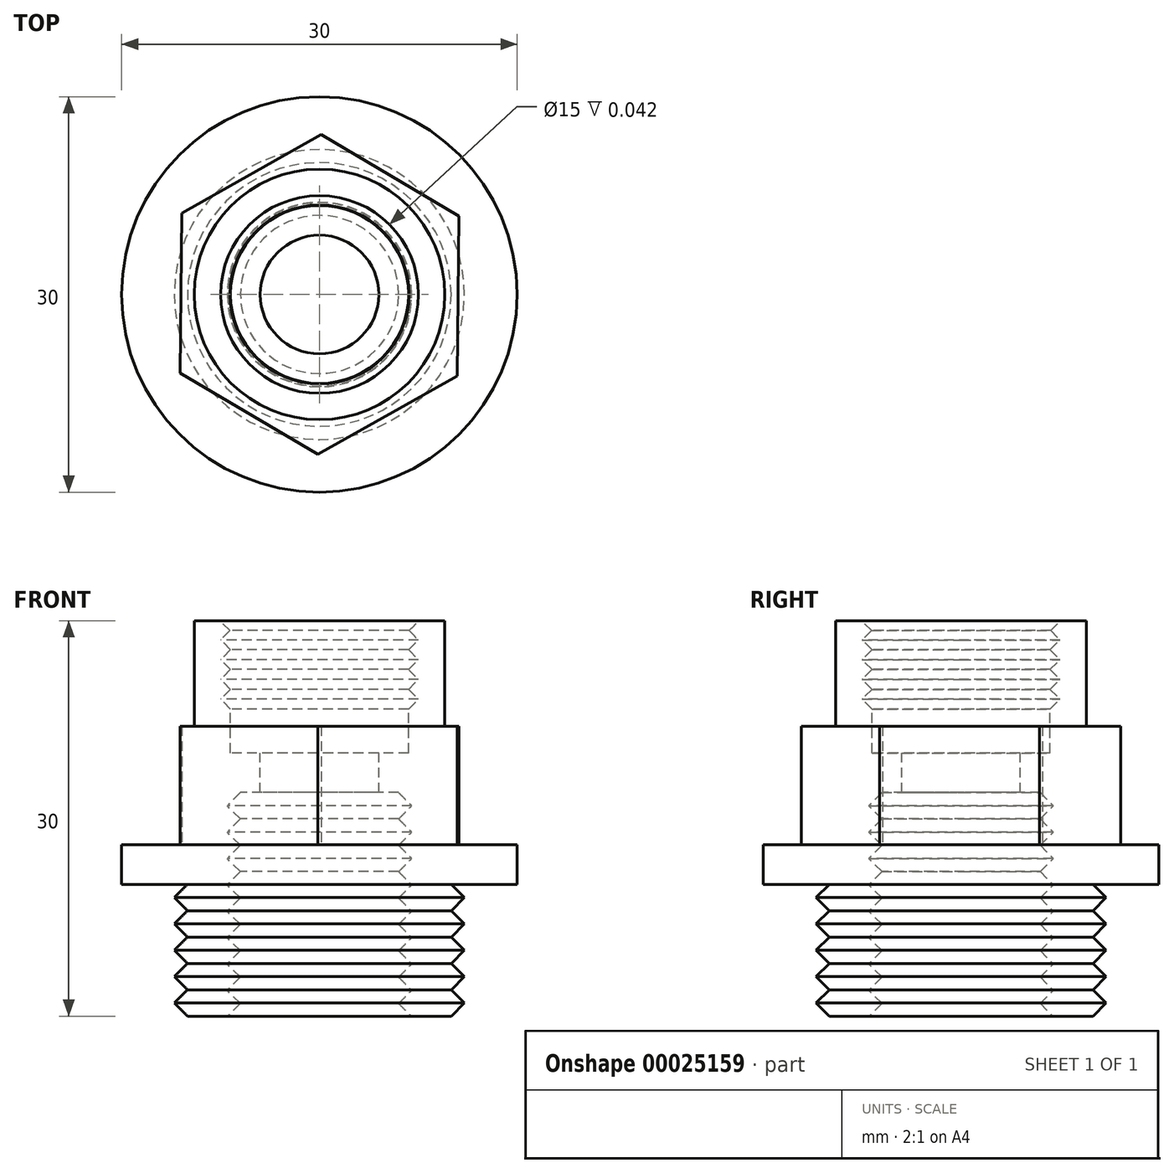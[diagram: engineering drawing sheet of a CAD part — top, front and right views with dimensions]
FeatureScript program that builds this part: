
annotation { "Feature Type Name" : "Feature", "Feature Type Description" : "" }
export const myFeature = defineFeature(function(context is Context, id is Id, definition is map)
    precondition{}
    {
        {
            var Q0;
            Q0=qCreatedBy(makeId("Front.planeOp"),FACE);
            var sketch = newSketch(context, id + "F0", { "sketchPlane" : qUnion([Q0])});
            skLineSegment(sketch, "E0", {"start": v(-0.01, -0.04) * mm, "end": v(-0.01, 28.34) * mm});
            skLineSegment(sketch, "E1", {"start": v(-0.01, -0.04) * mm, "end": v(-6.01, -0.04) * mm});
            skLineSegment(sketch, "E2", {"start": v(-10.01, 28.34) * mm, "end": v(-11.01, 27.34) * mm});
            skLineSegment(sketch, "E3.0.1.0", {"start": v(-11.01, 27.34) * mm, "end": v(-10.01, 26.34) * mm});
            skLineSegment(sketch, "E3.0.2.0", {"start": v(-11.01, 25.34) * mm, "end": v(-10.01, 24.34) * mm});
            skLineSegment(sketch, "E3.0.2.1", {"start": v(-10.01, 24.34) * mm, "end": v(-11.01, 23.34) * mm});
            skLineSegment(sketch, "E3.0.3.0", {"start": v(-11.01, 23.34) * mm, "end": v(-10.01, 22.34) * mm});
            skLineSegment(sketch, "E3.0.3.1", {"start": v(-10.01, 22.34) * mm, "end": v(-11.01, 21.34) * mm});
            skLineSegment(sketch, "E3.0.4.0", {"start": v(-11.01, 21.34) * mm, "end": v(-10.01, 20.34) * mm});
            skLineSegment(sketch, "E3.0.4.1", {"start": v(-10.01, 20.34) * mm, "end": v(-11.01, 19.34) * mm});
            skLineSegment(sketch, "E3.0.5.0", {"start": v(-11.01, 19.34) * mm, "end": v(-10.01, 18.34) * mm});
            skPoint(sketch, "E4.end.orphan", {"position": v(-10.01, -0.04) * mm});
            skPoint(sketch, "E5.orphan", {"position": v(-77.82, -0.04) * mm});
            skLineSegment(sketch, "E6.trimOffspring", {"start": v(-10.01, 26.34) * mm, "end": v(-11.01, 25.34) * mm});
            skLineSegment(sketch, "E7", {"start": v(-10.01, 18.34) * mm, "end": v(-0.01, 18.34) * mm});
            skLineSegment(sketch, "E8", {"start": v(-0.01, 28.34) * mm, "end": v(0, 28.34) * mm});
            skLineSegment(sketch, "E9", {"start": v(-15.01, 31.34) * mm, "end": v(-15.01, 28.34) * mm});
            skLineSegment(sketch, "E10", {"start": v(-10.01, 28.34) * mm, "end": v(-15.01, 28.34) * mm});
            skLineSegment(sketch, "E11", {"start": v(-0.01, 28.34) * mm, "end": v(-0.01, 48.74) * mm});
            skLineSegment(sketch, "E12", {"start": v(-15.01, 31.34) * mm, "end": v(0, 31.34) * mm});
            skSolve(sketch);
        }
        {
            var Q0;
            Q0 = qSketchRegion(id + "F0", true);
            var Q1;
            Q1=sQuery(id+"F0.wireOp",EDGE,"E0");
            revolve(context, id + "F1", {"entities" : qUnion([Q0]), "axis" : qUnion([Q1]), "revolveType" : RevolveType.FULL});
        }
        {
            var Q0;
            Q0=makeQuery(id+"F1.opRevolve","SWEPT_FACE",FACE,{"disambiguationData":[OSD([sQuery(id+"F0.wireOp",EDGE,"E12")])]});
            var sketch = newSketch(context, id + "F2", { "sketchPlane" : qUnion([Q0])});
            skCircle(sketch, "E13.cCircle", {"center": v(0, 0) * mm, "radius": 10.5 * mm, "construction": true});
            skLineSegment(sketch, "E13.0", {"start": v(0.13, 12.12) * mm, "end": v(10.56, 5.95) * mm});
            skLineSegment(sketch, "E13.1", {"start": v(10.56, 5.95) * mm, "end": v(10.44, -6.17) * mm});
            skLineSegment(sketch, "E13.2", {"start": v(10.44, -6.17) * mm, "end": v(-0.13, -12.12) * mm});
            skLineSegment(sketch, "E13.3", {"start": v(-0.13, -12.12) * mm, "end": v(-10.56, -5.95) * mm});
            skLineSegment(sketch, "E13.4", {"start": v(-10.56, -5.95) * mm, "end": v(-10.44, 6.17) * mm});
            skLineSegment(sketch, "E13.5", {"start": v(-10.44, 6.17) * mm, "end": v(0.13, 12.12) * mm});
            skPoint(sketch, "E13.0.midPoint", {"position": v(5.34, 9.04) * mm});
            skSolve(sketch);
        }
        {
            var Q0;
            Q0 = qSketchRegion(id + "F2", true);
            extrude(context, id + "F3", {"entities" : qUnion([Q0]), "operationType" : NewBodyOperationType.ADD, "depth" : 9 * mm});
        }
        {
            var Q0;
            Q0=makeQuery(id+"F3.opExtrude","CAP_FACE",FACE,{"disambiguationData":[OSD([sQuery(id+"F2.wireOp",EDGE,"E13.0"),sQuery(id+"F2.wireOp",EDGE,"E13.1"),sQuery(id+"F2.wireOp",EDGE,"E13.2"),sQuery(id+"F2.wireOp",EDGE,"E13.3"),sQuery(id+"F2.wireOp",EDGE,"E13.4"),sQuery(id+"F2.wireOp",EDGE,"E13.5")])],"isStart":false});
            var sketch = newSketch(context, id + "F4", { "sketchPlane" : qUnion([Q0])});
            skCircle(sketch, "E14", {"center": v(0, 0) * mm, "radius": 9.5 * mm});
            skSolve(sketch);
        }
        {
            var Q0;
            Q0 = qSketchRegion(id + "F4", true);
            extrude(context, id + "F5", {"entities" : qUnion([Q0]), "operationType" : NewBodyOperationType.ADD, "depth" : 8 * mm});
        }
        {
            var Q0;
            Q0=qCreatedBy(makeId("Front.planeOp"),FACE);
            var sketch = newSketch(context, id + "F6", { "sketchPlane" : qUnion([Q0])});
            skLineSegment(sketch, "E15", {"start": v(0, 17.48) * mm, "end": v(0, 52.95) * mm});
            skLineSegment(sketch, "E16", {"start": v(0, 0) * mm, "end": v(35.36, 0) * mm});
            skLineSegment(sketch, "E17", {"start": v(6, 38.3) * mm, "end": v(6.75, 38.3) * mm});
            skLineSegment(sketch, "E18", {"start": v(7.5, 48.3) * mm, "end": v(6.8, 47.6) * mm});
            skLineSegment(sketch, "E19", {"start": v(6.8, 47.6) * mm, "end": v(7.5, 46.88) * mm});
            skLineSegment(sketch, "E20", {"start": v(7.5, 46.88) * mm, "end": v(6.75, 46.13) * mm});
            skLineSegment(sketch, "E21", {"start": v(6.75, 46.13) * mm, "end": v(7.5, 45.38) * mm});
            skLineSegment(sketch, "E22", {"start": v(7.5, 45.38) * mm, "end": v(6.75, 44.63) * mm});
            skLineSegment(sketch, "E23", {"start": v(6.75, 44.63) * mm, "end": v(7.5, 43.88) * mm});
            skLineSegment(sketch, "E24", {"start": v(7.5, 43.88) * mm, "end": v(6.75, 43.13) * mm});
            skLineSegment(sketch, "E25", {"start": v(6.75, 43.13) * mm, "end": v(7.5, 42.38) * mm});
            skLineSegment(sketch, "E26", {"start": v(7.5, 42.38) * mm, "end": v(6.75, 41.63) * mm});
            skLineSegment(sketch, "E27.trimOffspring", {"start": v(7.5, 48.3) * mm, "end": v(7.5, 52.95) * mm});
            skLineSegment(sketch, "E28", {"start": v(6.75, 40.38) * mm, "end": v(6.75, 38.3) * mm});
            skLineSegment(sketch, "E29", {"start": v(6.75, 40.38) * mm, "end": v(6.75, 41.63) * mm});
            skLineSegment(sketch, "E30", {"start": v(4.5, 38.3) * mm, "end": v(4.5, 35.3) * mm});
            skPoint(sketch, "E31.orphan", {"position": v(0, 38.3) * mm});
            skLineSegment(sketch, "E32", {"start": v(6, 37.3) * mm, "end": v(6, 37.32) * mm});
            skLineSegment(sketch, "E33", {"start": v(7, 18.3) * mm, "end": v(6, 19.3) * mm});
            skLineSegment(sketch, "E34", {"start": v(6, 19.3) * mm, "end": v(7, 20.3) * mm});
            skLineSegment(sketch, "E35.0.1.0", {"start": v(6, 21.3) * mm, "end": v(7, 22.3) * mm});
            skLineSegment(sketch, "E35.0.1.1", {"start": v(7, 20.3) * mm, "end": v(6, 21.3) * mm});
            skLineSegment(sketch, "E35.0.2.0", {"start": v(6, 23.3) * mm, "end": v(7, 24.3) * mm});
            skLineSegment(sketch, "E35.0.2.1", {"start": v(7, 22.3) * mm, "end": v(6, 23.3) * mm});
            skLineSegment(sketch, "E35.0.3.0", {"start": v(6, 25.3) * mm, "end": v(7, 26.3) * mm});
            skLineSegment(sketch, "E35.0.3.1", {"start": v(7, 24.3) * mm, "end": v(6, 25.3) * mm});
            skLineSegment(sketch, "E35.0.4.0", {"start": v(6, 27.3) * mm, "end": v(7, 28.3) * mm});
            skLineSegment(sketch, "E35.0.4.1", {"start": v(7, 26.3) * mm, "end": v(6, 27.3) * mm});
            skLineSegment(sketch, "E35.0.5.0", {"start": v(6, 29.3) * mm, "end": v(7, 30.3) * mm});
            skLineSegment(sketch, "E35.0.5.1", {"start": v(7, 28.3) * mm, "end": v(6, 29.3) * mm});
            skLineSegment(sketch, "E35.0.6.0", {"start": v(6, 31.3) * mm, "end": v(7, 32.3) * mm});
            skLineSegment(sketch, "E35.0.6.1", {"start": v(7, 30.3) * mm, "end": v(6, 31.3) * mm});
            skLineSegment(sketch, "E35.0.7.0", {"start": v(6, 33.3) * mm, "end": v(7, 34.3) * mm});
            skLineSegment(sketch, "E35.0.7.1", {"start": v(7, 32.3) * mm, "end": v(6, 33.3) * mm});
            skLineSegment(sketch, "E35.0.8.1", {"start": v(7, 34.3) * mm, "end": v(6, 35.3) * mm});
            skLineSegment(sketch, "E36", {"start": v(6, 38.3) * mm, "end": v(4.5, 38.3) * mm});
            skLineSegment(sketch, "E37", {"start": v(6, 35.3) * mm, "end": v(4.5, 35.3) * mm});
            skLineSegment(sketch, "E38", {"start": v(7.5, 52.95) * mm, "end": v(0, 52.95) * mm});
            skPoint(sketch, "E39.orphan", {"position": v(0, 76.6) * mm});
            skLineSegment(sketch, "E40", {"start": v(7, 18.3) * mm, "end": v(7, 17.48) * mm});
            skLineSegment(sketch, "E41", {"start": v(7, 17.48) * mm, "end": v(0, 17.48) * mm});
            skSolve(sketch);
        }
        {
            var Q0;
            Q0 = qSketchRegion(id + "F6", true);
            var Q1;
            Q1=sQuery(id+"F6.wireOp",EDGE,"E15");
            revolve(context, id + "F7", {"operationType" : NewBodyOperationType.REMOVE, "entities" : qUnion([Q0]), "axis" : qUnion([Q1]), "revolveType" : RevolveType.FULL, "oppositeDirection" : true});
        }
    });
